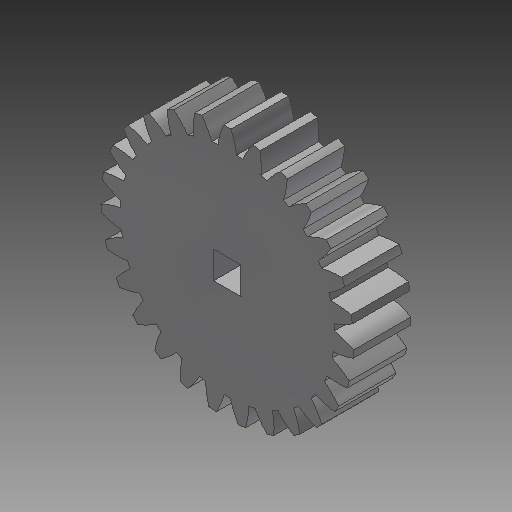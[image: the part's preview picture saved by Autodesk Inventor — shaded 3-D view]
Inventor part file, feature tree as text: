
AUTODESK INVENTOR PART (.ipt)
format: ipt  version: 2017 (Build 210142000, 142)  size: 260,608 bytes
history: native  units: mm (DEFAULTED — no unit token found)
features: plane x3, other x3, sketch x3, extrude x2
ambient origin geometry x8: Origin, YZ Plane, XZ Plane, XY Plane, X Axis, Y Axis, Z Axis, Center Point
bodies: Solid1 (feature_tree)
feature tree (11):
  extrude  "Extrusion1"  Depth=20.0mm TaperAngle=0.0deg
  plane  "Work Plane2"
  plane  "Work Plane8"
  plane  "Work Plane9"
  other  "Spur Gear"
  extrude  "Extrusion2"  Depth=10.0mm TaperAngle=0.0deg
  sketch  "Sketch1"  dims[d0=88.0mm d1=20.0mm d2=0.0mm]
  sketch  "Sketch2"  dims[d3=81.509434mm d4=10.0mm d5=0.0mm]
  other  "Srf1"
  sketch  "Sketch3"  dims[d16=80.0mm d17=0.0mm d34=1.163553mm d39=0.0mm d41=0.0mm d43=80.0mm d46=80.0mm d47=0.0mm d48=0.0mm d49=9.525mm d50=10.0mm d51=0.0mm]
  other  "Pitch Diameter"
